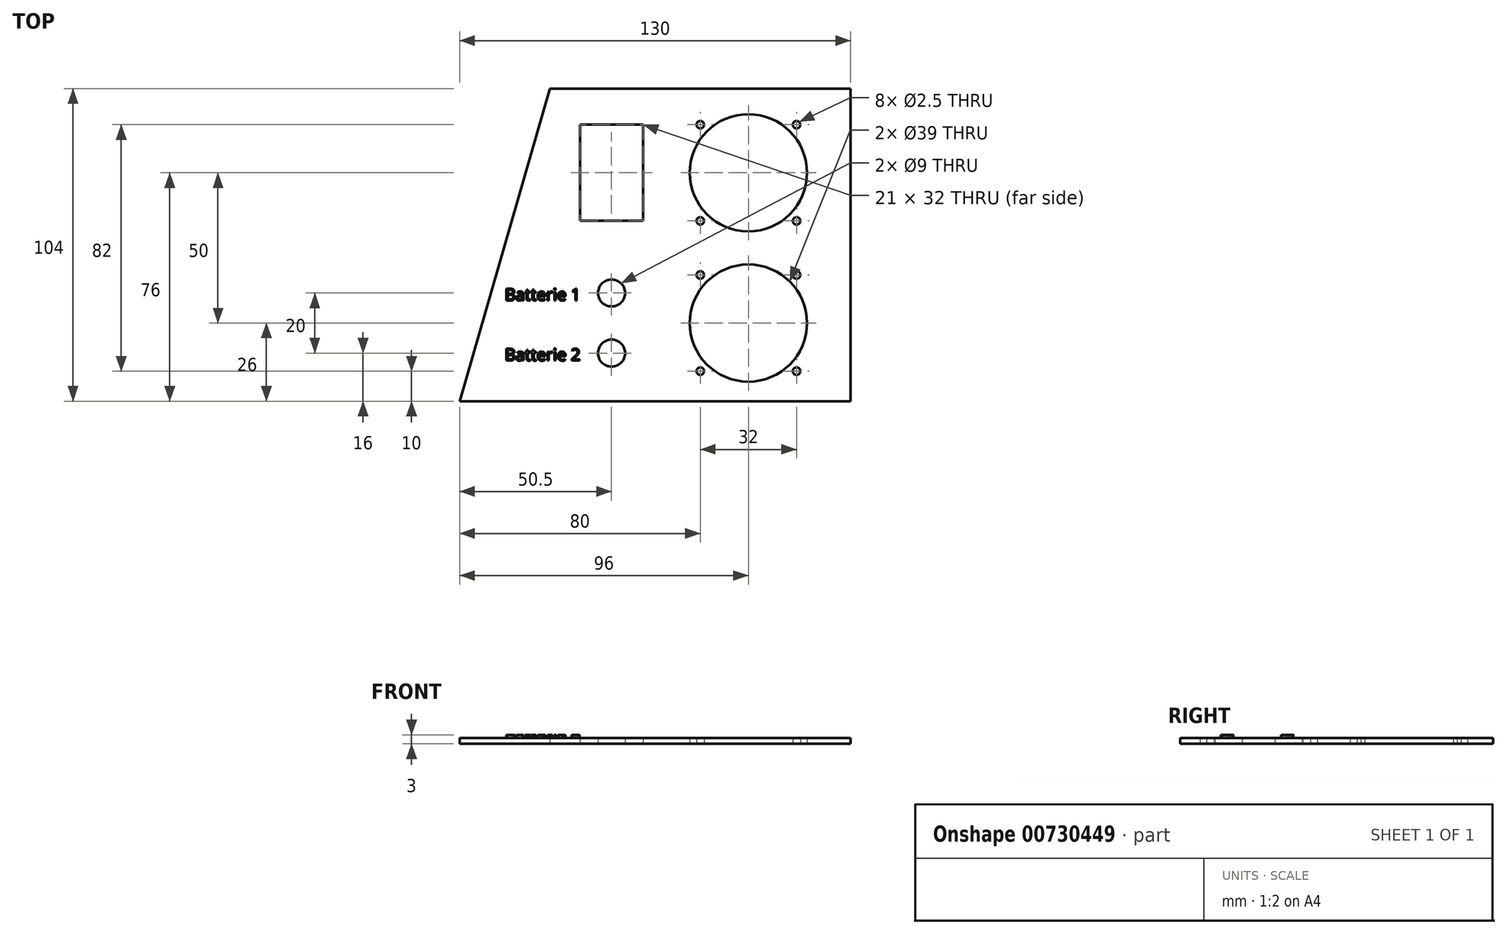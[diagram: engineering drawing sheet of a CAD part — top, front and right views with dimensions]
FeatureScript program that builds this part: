
annotation { "Feature Type Name" : "Feature", "Feature Type Description" : "" }
export const myFeature = defineFeature(function(context is Context, id is Id, definition is map)
    precondition{}
    {
        {
            var Q0;
            Q0=qCreatedBy(makeId("Top.planeOp"),FACE);
            var sketch = newSketch(context, id + "F0", { "sketchPlane" : qUnion([Q0])});
            skLineSegment(sketch, "E0", {"start": v(0, 0) * mm, "end": v(130, 0) * mm});
            skLineSegment(sketch, "E1", {"start": v(130, 0) * mm, "end": v(130, 104) * mm});
            skLineSegment(sketch, "E2", {"start": v(130, 104) * mm, "end": v(30, 104) * mm});
            skLineSegment(sketch, "E3", {"start": v(30, 104) * mm, "end": v(0, 0) * mm});
            skPoint(sketch, "E4", {"position": v(80, 92) * mm});
            skPoint(sketch, "E5", {"position": v(112, 92) * mm});
            skPoint(sketch, "E6", {"position": v(112, 60) * mm});
            skPoint(sketch, "E7", {"position": v(80, 60) * mm});
            skCircle(sketch, "E8", {"center": v(96, 76) * mm, "radius": 19.5 * mm});
            skCircle(sketch, "E9.0.1.0", {"center": v(96, 26) * mm, "radius": 19.5 * mm});
            skPoint(sketch, "E9.0.1.1", {"position": v(80, 42) * mm});
            skPoint(sketch, "E9.0.1.2", {"position": v(112, 42) * mm});
            skPoint(sketch, "E9.0.1.3", {"position": v(112, 10) * mm});
            skPoint(sketch, "E9.0.1.4", {"position": v(80, 10) * mm});
            skLineSegment(sketch, "E9.direction1", {"start": v(80, 60) * mm, "end": v(171, 60) * mm, "construction": true});
            skLineSegment(sketch, "E9.direction2", {"start": v(80, 60) * mm, "end": v(80, 10) * mm, "construction": true});
            skLineSegment(sketch, "E10.bottom", {"start": v(40, 92) * mm, "end": v(61, 92) * mm});
            skLineSegment(sketch, "E10.top", {"start": v(40, 60) * mm, "end": v(61, 60) * mm});
            skLineSegment(sketch, "E10.left", {"start": v(40, 92) * mm, "end": v(40, 60) * mm});
            skLineSegment(sketch, "E10.right", {"start": v(61, 92) * mm, "end": v(61, 60) * mm});
            skCircle(sketch, "E11", {"center": v(50.5, 36) * mm, "radius": 4.5 * mm});
            skCircle(sketch, "E12", {"center": v(50.5, 16) * mm, "radius": 4.5 * mm});
            skSolve(sketch);
        }
        {
            var Q0;
            Q0 = qSketchRegion(id + "F0", true);
            extrude(context, id + "F1", {"entities" : qUnion([Q0]), "depth" : 2 * mm, "offsetDistance" : 25 * mm});
        }
        {
            var Q0;
            Q0=sQuery(id+"F0.wireOp",VERTEX,"E5");
            var Q1;
            Q1=sQuery(id+"F0.wireOp",VERTEX,"E4");
            var Q2;
            Q2=sQuery(id+"F0.wireOp",VERTEX,"E7");
            var Q3;
            Q3=sQuery(id+"F0.wireOp",VERTEX,"E6");
            var Q4;
            Q4=sQuery(id+"F0.wireOp",VERTEX,"E9.0.1.2");
            var Q5;
            Q5=sQuery(id+"F0.wireOp",VERTEX,"E9.0.1.1");
            var Q6;
            Q6=sQuery(id+"F0.wireOp",VERTEX,"E9.0.1.4");
            var Q7;
            Q7=sQuery(id+"F0.wireOp",VERTEX,"E9.0.1.3");
            var Q8;
            Q8=makeQuery(id+"F1.opExtrude","SWEPT_BODY",BODY,{"disambiguationData":[OSD([sQuery(id+"F0.wireOp",EDGE,"E0"),sQuery(id+"F0.wireOp",EDGE,"E1"),sQuery(id+"F0.wireOp",EDGE,"E2"),sQuery(id+"F0.wireOp",EDGE,"E3"),sQuery(id+"F0.wireOp",EDGE,"E8"),sQuery(id+"F0.wireOp",EDGE,"E9.0.1.0")])]});
            hole(context, id + "F2", {"style" : HoleStyle.SIMPLE, "endStyle" : HoleEndStyle.THROUGH, "oppositeDirection" : true, "holeDiameter" : 2.5 * mm, "majorDiameter" : 5 * mm, "isTappedThrough" : true, "tappedDepth" : 12 * mm, "tapClearance" : 3, "locations" : qUnion([Q0, Q1, Q2, Q3, Q4, Q5, Q6, Q7]), "scope" : qUnion([Q8])});
        }
        {
            var Q0;
            Q0=qCreatedBy(makeId("Top.planeOp"),FACE);
            var sketch = newSketch(context, id + "F3", { "sketchPlane" : qUnion([Q0])});
            skText(sketch, "E13", { "text": "Batterie 1", "fontName": "OpenSans-Regular.ttf"});
            skText(sketch, "E14", { "text": "Batterie 2", "fontName": "OpenSans-Regular.ttf"});
            const initialGuessF3  = {"E13": [0.015, 0.0335, 1, 0, 0.004], "E14": [0.015, 0.0135, 1, 0, 0.004]};
            skSetInitialGuess(sketch, initialGuessF3);
            skSolve(sketch);
        }
        {
            var Q0;
            Q0 = qSketchRegion(id + "F3", true);
            extrude(context, id + "F4", {"entities" : qUnion([Q0]), "operationType" : NewBodyOperationType.ADD, "depth" : 3 * mm, "offsetDistance" : 25 * mm});
        }
    });
